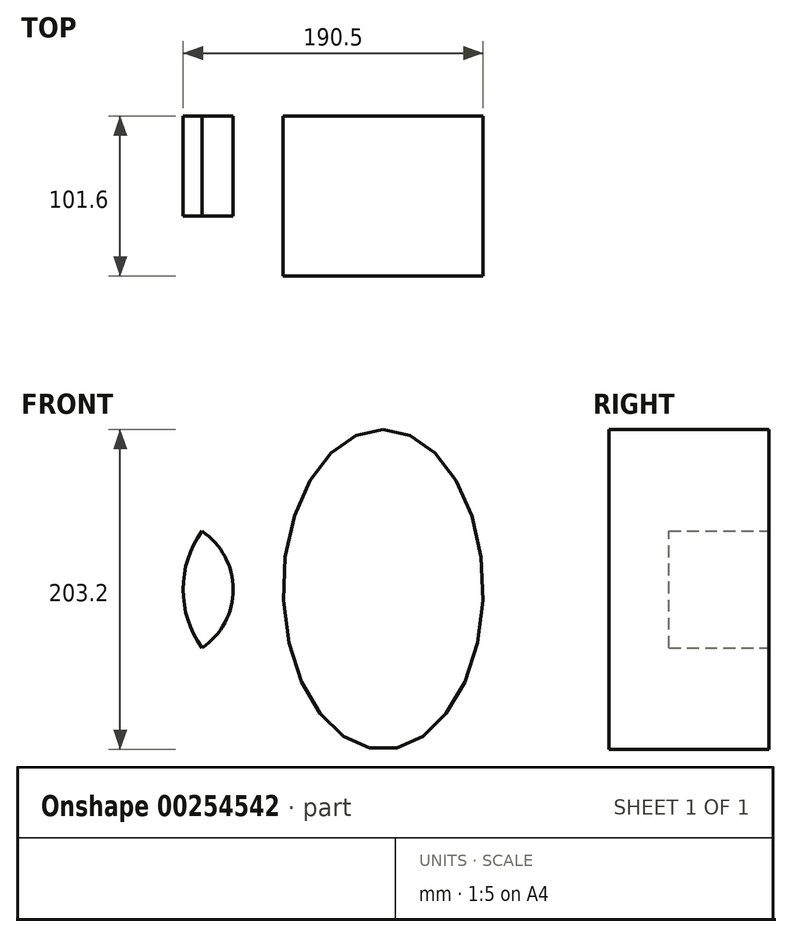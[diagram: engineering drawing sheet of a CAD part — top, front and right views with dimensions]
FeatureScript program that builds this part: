
annotation { "Feature Type Name" : "Feature", "Feature Type Description" : "" }
export const myFeature = defineFeature(function(context is Context, id is Id, definition is map)
    precondition{}
    {
        {
            var Q0;
            Q0=qCreatedBy(makeId("Front.planeOp"),FACE);
            var sketch = newSketch(context, id + "F0", { "sketchPlane" : qUnion([Q0])});
            skLineSegment(sketch, "E0", {"start": v(0, 0) * mm, "end": v(-76.2, 0) * mm});
            skCircle(sketch, "E1", {"center": v(-76.2, 0) * mm, "radius": 44.45 * mm});
            skLineSegment(sketch, "E2", {"start": v(-31.75, 0) * mm, "end": v(-63.5, 0) * mm});
            skCircle(sketch, "E3", {"center": v(0, 0) * mm, "radius": 63.5 * mm});
            skLineSegment(sketch, "E4", {"start": v(63.5, 0) * mm, "end": v(63.5, 101.6) * mm});
            skEllipse(sketch, "E5", {"center": v(63.5, 0) * mm, "majorRadius": 101.6 * mm, "minorRadius": 63.5 * mm, "majorAxis": v(0, 1)});
            skSolve(sketch);
        }
        {
            var Q0;
            {var subQ0=sQuery(id+"F0.wireOp",EDGE,"E3");var subQ1=sQuery(id+"F0.wireOp",EDGE,"E1");var subQ2=makeQuery(id+"F0.imprint","INTERSECT",VERTEX,{"disambiguationData":[OD(0.0)],"derivedFrom":[subQ1,subQ0]});Q0=makeQuery(id+"F0.imprint","IMPRINT",FACE,{"disambiguationData":[TD([[makeQuery(id+"F0.imprint","IMPRINT",EDGE,{"disambiguationData":[TD([[subQ2,-1.0]])],"derivedFrom":subQ1}),1.0]])]});}
            extrude(context, id + "F1", {"entities" : qUnion([Q0]), "depth" : 25.4 * mm});
        }
        {
            var Q0;
            {var subQ3=sQuery(id+"F0.wireOp",EDGE,"E1");var subQ5=sQuery(id+"F0.wireOp",EDGE,"E3");var subQ6=makeQuery(id+"F0.imprint","INTERSECT",VERTEX,{"disambiguationData":[OD(0.0)],"derivedFrom":[subQ3,subQ5]});Q0=makeQuery(id+"F0.imprint","IMPRINT",FACE,{"disambiguationData":[TD([[makeQuery(id+"F0.imprint","IMPRINT",EDGE,{"disambiguationData":[TD([[subQ6,1.0]])],"derivedFrom":subQ5}),1.0]])]});}
            var Q1;
            {var subQ0=sQuery(id+"F0.wireOp",EDGE,"E2");Q1=makeQuery(id+"F0.imprint","IMPRINT",FACE,{"disambiguationData":[TD([[makeQuery(id+"F0.imprint","IMPRINT",EDGE,{"derivedFrom":subQ0}),-1.0]])]});}
            var Q2;
            {var subQ0=sQuery(id+"F0.wireOp",EDGE,"E2");Q2=makeQuery(id+"F0.imprint","IMPRINT",FACE,{"disambiguationData":[TD([[makeQuery(id+"F0.imprint","IMPRINT",EDGE,{"derivedFrom":subQ0}),1.0]])]});}
            var Q3;
            {var subQ3=sQuery(id+"F0.wireOp",EDGE,"E1");var subQ5=sQuery(id+"F0.wireOp",EDGE,"E3");var subQ6=makeQuery(id+"F0.imprint","INTERSECT",VERTEX,{"disambiguationData":[OD(1.0)],"derivedFrom":[subQ3,subQ5]});Q3=makeQuery(id+"F0.imprint","IMPRINT",FACE,{"disambiguationData":[TD([[makeQuery(id+"F0.imprint","IMPRINT",EDGE,{"disambiguationData":[TD([[subQ6,-1.0]])],"derivedFrom":subQ5}),1.0]])]});}
            extrude(context, id + "F2", {"entities" : qUnion([Q0, Q1, Q2, Q3]), "operationType" : NewBodyOperationType.ADD, "depth" : 63.5 * mm});
        }
        {
            var Q0;
            {var subQ0=sQuery(id+"F0.wireOp",EDGE,"E4");Q0=makeQuery(id+"F0.imprint","IMPRINT",FACE,{"disambiguationData":[TD([[makeQuery(id+"F0.imprint","IMPRINT",EDGE,{"derivedFrom":subQ0}),-1.0]])]});}
            var Q1;
            {var subQ0=sQuery(id+"F0.wireOp",EDGE,"E3");var subQ1=makeQuery(id+"F0.imprint","INTERSECT",VERTEX,{"derivedFrom":[subQ0,sQuery(id+"F0.wireOp",EDGE,"E4")]});Q1=makeQuery(id+"F0.imprint","IMPRINT",FACE,{"disambiguationData":[TD([[makeQuery(id+"F0.imprint","IMPRINT",EDGE,{"disambiguationData":[TD([[subQ1,-1.0]])],"derivedFrom":subQ0}),1.0]])]});}
            var Q2;
            {var subQ0=sQuery(id+"F0.wireOp",EDGE,"E4");Q2=makeQuery(id+"F0.imprint","IMPRINT",FACE,{"disambiguationData":[TD([[makeQuery(id+"F0.imprint","IMPRINT",EDGE,{"derivedFrom":subQ0}),1.0]])]});}
            extrude(context, id + "F3", {"entities" : qUnion([Q0, Q1, Q2]), "operationType" : NewBodyOperationType.ADD, "depth" : 101.6 * mm});
        }
    });
